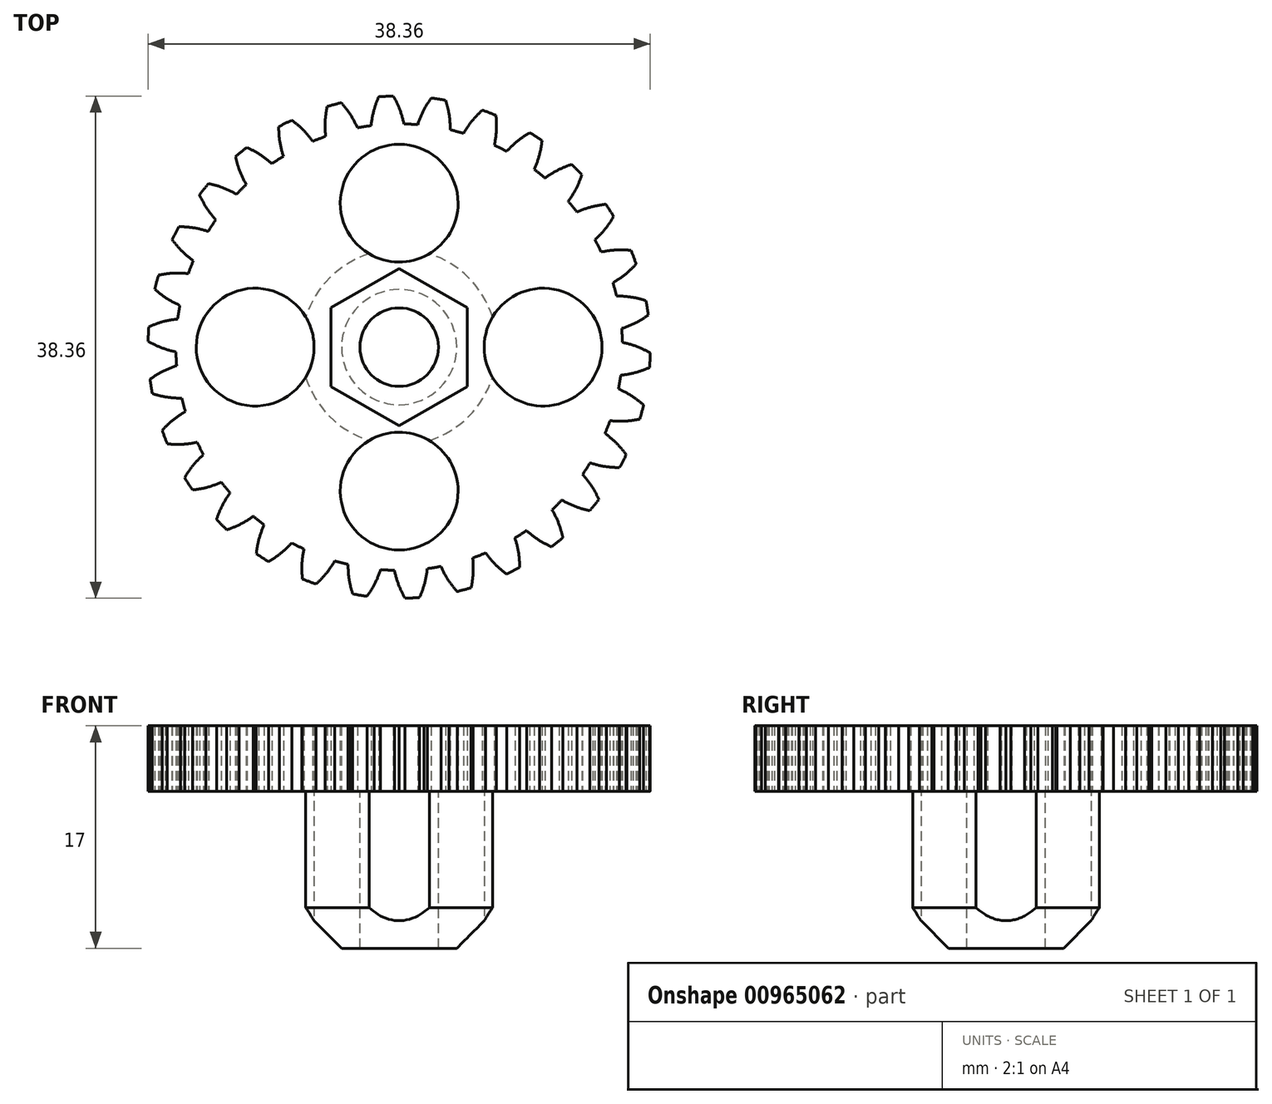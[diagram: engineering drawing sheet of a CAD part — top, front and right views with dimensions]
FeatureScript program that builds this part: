
annotation { "Feature Type Name" : "Feature", "Feature Type Description" : "" }
export const myFeature = defineFeature(function(context is Context, id is Id, definition is map)
    precondition{}
    {
        {
            var Q0;
            Q0=qCreatedBy(makeId("Top.planeOp"),FACE);
            var sketch = newSketch(context, id + "F0", { "sketchPlane" : qUnion([Q0])});
            skCircle(sketch, "E0", {"center": v(0, 0) * mm, "radius": 17.06 * mm});
            skCircle(sketch, "E1", {"center": v(0, 0) * mm, "radius": 18.27 * mm, "construction": true});
            skCircle(sketch, "E2", {"center": v(0, 0) * mm, "radius": 19.19 * mm, "construction": true});
            skLineSegment(sketch, "E3", {"start": v(0, 0) * mm, "end": v(0, 27.2) * mm, "construction": true});
            skLineSegment(sketch, "E4", {"start": v(0, 0) * mm, "end": v(-1.42, 27.13) * mm, "construction": true});
            skLineSegment(sketch, "E5", {"start": v(0, 18.27) * mm, "end": v(-22.3, 18.27) * mm, "construction": true});
            skLineSegment(sketch, "E6", {"start": v(0, 18.27) * mm, "end": v(-22.74, 9.09) * mm, "construction": true});
            skLineSegment(sketch, "E7", {"start": v(0, 0) * mm, "end": v(-6.35, 15.71) * mm, "construction": true});
            skCircle(sketch, "E8", {"center": v(0, 0) * mm, "radius": 16.94 * mm, "construction": true});
            skCircle(sketch, "E9", {"center": v(0, 18.27) * mm, "radius": 6.85 * mm, "construction": true});
            skCircle(sketch, "E10", {"center": v(-6.35, 15.71) * mm, "radius": 6.85 * mm, "construction": true});
            skArc(sketch, "E11", {"start": v(0, 18.27) * mm, "mid": v(-0.21, 18.74) * mm, "end": v(-0.45, 19.18) * mm});
            skArc(sketch, "E12", {"start": v(0.37, 17.05) * mm, "mid": v(0.2, 17.67) * mm, "end": v(0, 18.27) * mm});
            skArc(sketch, "E13.MirrorCS", {"start": v(-1.91, 18.17) * mm, "mid": v(-1.75, 18.65) * mm, "end": v(-1.56, 19.13) * mm});
            skArc(sketch, "E14.MirrorCS", {"start": v(-2.15, 16.92) * mm, "mid": v(-2.05, 17.55) * mm, "end": v(-1.91, 18.17) * mm});
            skArc(sketch, "E15", {"start": v(-0.45, 19.18) * mm, "mid": v(-1, 19.16) * mm, "end": v(-1.56, 19.13) * mm});
            skCircle(sketch, "E16", {"center": v(0, 0) * mm, "radius": 3 * mm});
            skCircle(sketch, "E17.cCircle", {"center": v(0, 0) * mm, "radius": 5.2 * mm, "construction": true});
            skLineSegment(sketch, "E17.0", {"start": v(5.2, -3) * mm, "end": v(0, -6) * mm});
            skLineSegment(sketch, "E17.1", {"start": v(0, -6) * mm, "end": v(-5.2, -3) * mm});
            skLineSegment(sketch, "E17.2", {"start": v(-5.2, -3) * mm, "end": v(-5.2, 3) * mm});
            skLineSegment(sketch, "E17.3", {"start": v(-5.2, 3) * mm, "end": v(0, 6) * mm});
            skLineSegment(sketch, "E17.4", {"start": v(0, 6) * mm, "end": v(5.2, 3) * mm});
            skLineSegment(sketch, "E17.5", {"start": v(5.2, 3) * mm, "end": v(5.2, -3) * mm});
            skPoint(sketch, "E17.0.midPoint", {"position": v(2.6, -4.5) * mm});
            skCircle(sketch, "E18", {"center": v(11, 0) * mm, "radius": 4.5 * mm});
            skCircle(sketch, "E19", {"center": v(0, 11) * mm, "radius": 4.5 * mm});
            skCircle(sketch, "E20", {"center": v(0, -11) * mm, "radius": 4.5 * mm});
            skCircle(sketch, "E21", {"center": v(-11, 0) * mm, "radius": 4.5 * mm});
            skCircle(sketch, "E22", {"center": v(0, 0) * mm, "radius": 7.5 * mm});
            skSolve(sketch);
        }
        {
            var Q0;
            {var subQ0=sQuery(id+"F0.wireOp",EDGE,"E0");var subQ1=makeQuery(id+"F0.imprint","INTERSECT",VERTEX,{"derivedFrom":[subQ0,sQuery(id+"F0.wireOp",EDGE,"E12")]});Q0=makeQuery(id+"F0.imprint","IMPRINT",FACE,{"disambiguationData":[TD([[makeQuery(id+"F0.imprint","IMPRINT",EDGE,{"disambiguationData":[TD([[subQ1,-1.0]])],"derivedFrom":subQ0}),1.0]])]});}
            var Q1;
            Q1=makeQuery(id+"F0.imprint","IMPRINT",FACE,{"disambiguationData":[TD([[makeQuery(id+"F0.imprint","IMPRINT",EDGE,{"derivedFrom":sQuery(id+"F0.wireOp",EDGE,"E11")}),1.0]])]});
            var Q2;
            Q2=makeQuery(id+"F0.imprint","IMPRINT",FACE,{"disambiguationData":[TD([[makeQuery(id+"F0.imprint","IMPRINT",EDGE,{"derivedFrom":sQuery(id+"F0.wireOp",EDGE,"E17.0")}),1.0]])]});
            extrude(context, id + "F1", {"entities" : qUnion([Q0, Q1, Q2]), "depth" : 5 * mm, "offsetDistance" : 25 * mm});
        }
        {
            var Q0;
            Q0=makeQuery(id+"F1.opExtrude","SWEPT_FACE",FACE,{"disambiguationData":[OSD([sQuery(id+"F0.wireOp",EDGE,"E11")])]});
            var Q1;
            Q1=makeQuery(id+"F1.opExtrude","SWEPT_FACE",FACE,{"disambiguationData":[OSD([sQuery(id+"F0.wireOp",EDGE,"E15")])]});
            var Q2;
            Q2=makeQuery(id+"F1.opExtrude","SWEPT_FACE",FACE,{"disambiguationData":[OSD([sQuery(id+"F0.wireOp",EDGE,"E12")])]});
            var Q3;
            Q3=makeQuery(id+"F1.opExtrude","SWEPT_FACE",FACE,{"disambiguationData":[OSD([sQuery(id+"F0.wireOp",EDGE,"E13.MirrorCS")])]});
            var Q4;
            Q4=makeQuery(id+"F1.opExtrude","SWEPT_FACE",FACE,{"disambiguationData":[OSD([sQuery(id+"F0.wireOp",EDGE,"E14.MirrorCS")])]});
            var Q5;
            Q5=makeQuery(id+"F1.opExtrude","SWEPT_FACE",FACE,{"disambiguationData":[OSD([sQuery(id+"F0.wireOp",EDGE,"E0")])]});
            circularPattern(context, id + "F2", {"patternType" : PatternType.FACE, "faces" : qUnion([Q0, Q1, Q2, Q3, Q4]), "axis" : qUnion([Q5]), "angle" : 360 * degree, "instanceCount" : 30, "equalSpace" : true});
        }
        {
            var Q0;
            Q0=makeQuery(id+"F0.imprint","IMPRINT",FACE,{"disambiguationData":[TD([[makeQuery(id+"F0.imprint","IMPRINT",EDGE,{"derivedFrom":sQuery(id+"F0.wireOp",EDGE,"E17.0")}),1.0]])]});
            var Q1;
            Q1=makeQuery(id+"F0.imprint","IMPRINT",FACE,{"disambiguationData":[TD([[makeQuery(id+"F0.imprint","IMPRINT",EDGE,{"derivedFrom":sQuery(id+"F0.wireOp",EDGE,"E16")}),-1.0]])]});
            extrude(context, id + "F3", {"entities" : qUnion([Q0, Q1]), "operationType" : NewBodyOperationType.ADD, "oppositeDirection" : true, "depth" : 12 * mm, "offsetDistance" : 25 * mm});
        }
        {
            var Q0;
            {var subQ0=sQuery(id+"F0.wireOp",EDGE,"E22");Q0=makeQuery(id+"F3.opExtrude","CAP_EDGE",EDGE,{"disambiguationData":[OSD([subQ0]),TDD([makeQuery(id+"F0.imprint","IMPRINT",EDGE,{"disambiguationData":[TD([[makeQuery(id+"F0.imprint","INTERSECT",VERTEX,{"disambiguationData":[OD(1.0)],"derivedFrom":[sQuery(id+"F0.wireOp",EDGE,"E18"),subQ0]}),1.0]])],"derivedFrom":subQ0})])],"isStart":false});}
            var Q1;
            {var subQ0=sQuery(id+"F0.wireOp",EDGE,"E22");Q1=makeQuery(id+"F3.opExtrude","CAP_EDGE",EDGE,{"disambiguationData":[OSD([subQ0]),TDD([makeQuery(id+"F0.imprint","IMPRINT",EDGE,{"disambiguationData":[TD([[makeQuery(id+"F0.imprint","INTERSECT",VERTEX,{"disambiguationData":[OD(1.0)],"derivedFrom":[sQuery(id+"F0.wireOp",EDGE,"E18"),subQ0]}),1.0]])],"derivedFrom":subQ0})])],"isStart":true});}
            var Q2;
            {var subQ0=sQuery(id+"F0.wireOp",EDGE,"E22");Q2=makeQuery(id+"F3.opExtrude","CAP_EDGE",EDGE,{"disambiguationData":[OSD([subQ0]),TDD([makeQuery(id+"F0.imprint","IMPRINT",EDGE,{"disambiguationData":[TD([[makeQuery(id+"F0.imprint","INTERSECT",VERTEX,{"disambiguationData":[OD(1.0)],"derivedFrom":[sQuery(id+"F0.wireOp",EDGE,"E20"),subQ0]}),1.0]])],"derivedFrom":subQ0})])],"isStart":true});}
            var Q3;
            {var subQ0=sQuery(id+"F0.wireOp",EDGE,"E22");Q3=makeQuery(id+"F3.opExtrude","CAP_EDGE",EDGE,{"disambiguationData":[OSD([subQ0]),TDD([makeQuery(id+"F0.imprint","IMPRINT",EDGE,{"disambiguationData":[TD([[makeQuery(id+"F0.imprint","INTERSECT",VERTEX,{"disambiguationData":[OD(0.0)],"derivedFrom":[sQuery(id+"F0.wireOp",EDGE,"E19"),subQ0]}),-1.0]])],"derivedFrom":subQ0})])],"isStart":true});}
            var Q4;
            {var subQ0=sQuery(id+"F0.wireOp",EDGE,"E22");Q4=makeQuery(id+"F3.opExtrude","CAP_EDGE",EDGE,{"disambiguationData":[OSD([subQ0]),TDD([makeQuery(id+"F0.imprint","IMPRINT",EDGE,{"disambiguationData":[TD([[makeQuery(id+"F0.imprint","INTERSECT",VERTEX,{"disambiguationData":[OD(0.0)],"derivedFrom":[sQuery(id+"F0.wireOp",EDGE,"E18"),subQ0]}),-1.0]])],"derivedFrom":subQ0})])],"isStart":true});}
            chamfer(context, id + "F4", {"entities" : qUnion([Q0, Q1, Q2, Q3, Q4]), "chamferType" : ChamferType.OFFSET_ANGLE, "width" : 3.1 * mm, "oppositeDirection" : false, "angle" : 45 * degree});
        }
    });
